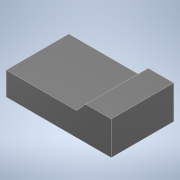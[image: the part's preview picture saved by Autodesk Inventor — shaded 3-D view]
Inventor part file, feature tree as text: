
AUTODESK INVENTOR PART (.ipt)
format: ipt  version: 2022 (Build 260153000, 153)  size: 95,744 bytes
history: native  units: in
note: dims shown in document units (in); Inventor stores cm internally (conversion verified against a paired STEP export)
features: extrude x1, sketch x1
ambient origin geometry x8: Origin, YZ Plane, XZ Plane, XY Plane, X Axis, Y Axis, Z Axis, Center Point
bodies: Solid1 (feature_tree)
feature tree (2):
  extrude  "Extrusion1"  Depth=1.8504in
  sketch  "Sketch1"  dims[d2=1.1024in d3=0.0in d4=1.8504in d5=0.5906in d6=0.4488in d7=0.4134in d8=1.2402in]
